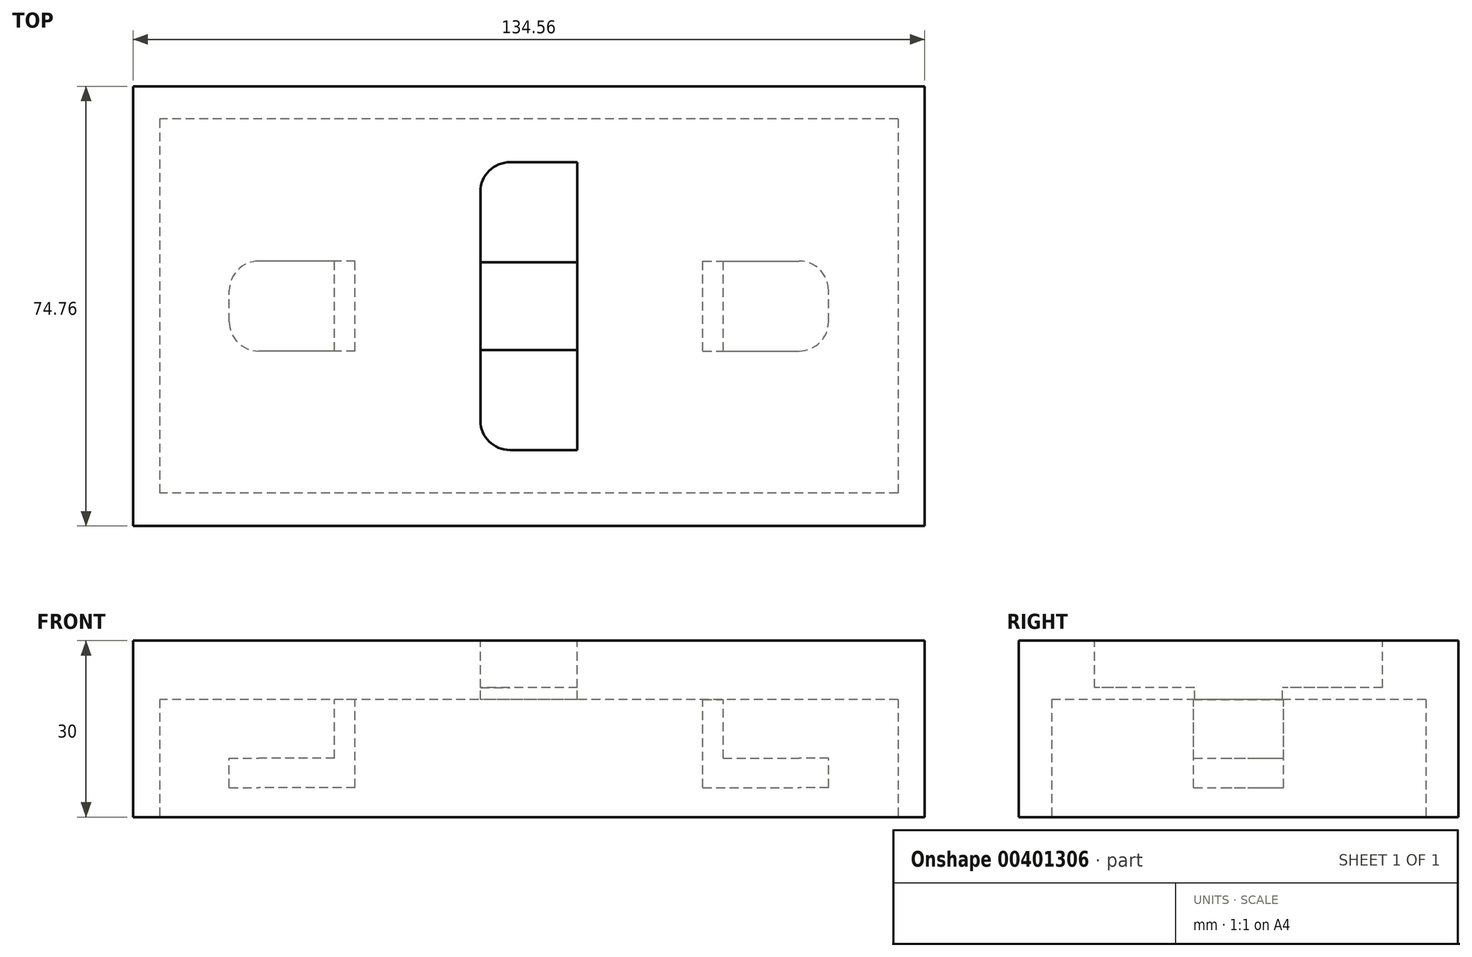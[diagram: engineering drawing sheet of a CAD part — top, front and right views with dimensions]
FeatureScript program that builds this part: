
annotation { "Feature Type Name" : "Feature", "Feature Type Description" : "" }
export const myFeature = defineFeature(function(context is Context, id is Id, definition is map)
    precondition{}
    {
        {
            var Q0;
            Q0=qCreatedBy(makeId("Top.planeOp"),FACE);
            var sketch = newSketch(context, id + "F0", { "sketchPlane" : qUnion([Q0])});
            skLineSegment(sketch, "E0.bottom", {"start": v(67.28, 37.38) * mm, "end": v(-67.28, 37.38) * mm});
            skLineSegment(sketch, "E0.top", {"start": v(67.28, -37.38) * mm, "end": v(-67.28, -37.38) * mm});
            skLineSegment(sketch, "E0.left", {"start": v(67.28, 37.38) * mm, "end": v(67.28, -37.38) * mm});
            skLineSegment(sketch, "E0.right", {"start": v(-67.28, 37.38) * mm, "end": v(-67.28, -37.38) * mm});
            skPoint(sketch, "E0.middle", {"position": v(0, 0) * mm});
            skSolve(sketch);
        }
        {
            var Q0;
            Q0=qSketchRegion(id+"F0",true);
            extrude(context, id + "F1", {"entities" : qUnion([Q0]), "depth" : 30 * mm});
        }
        {
            var Q0;
            Q0=makeQuery(id+"F1.opExtrude","CAP_FACE",FACE,{"disambiguationData":[OSD([sQuery(id+"F0.wireOp",EDGE,"E0.bottom"),sQuery(id+"F0.wireOp",EDGE,"E0.top"),sQuery(id+"F0.wireOp",EDGE,"E0.left"),sQuery(id+"F0.wireOp",EDGE,"E0.right")])],"isStart":false});
            var sketch = newSketch(context, id + "F2", { "sketchPlane" : qUnion([Q0])});
            skLineSegment(sketch, "E1.bottom", {"start": v(8.23, 24.47) * mm, "end": v(-3.23, 24.47) * mm});
            skLineSegment(sketch, "E1.top", {"start": v(8.23, -24.47) * mm, "end": v(-3.23, -24.47) * mm});
            skLineSegment(sketch, "E1.left", {"start": v(8.23, 24.47) * mm, "end": v(8.23, -24.47) * mm});
            skLineSegment(sketch, "E1.right", {"start": v(-8.23, 19.47) * mm, "end": v(-8.23, -19.47) * mm});
            skPoint(sketch, "E1.middle", {"position": v(0, 0) * mm});
            skPoint(sketch, "E2.visualSharp", {"position": v(-8.23, 24.47) * mm});
            skArc(sketch, "E2.filletArc", {"start": v(-3.23, 24.47) * mm, "mid": v(-6.77, 23) * mm, "end": v(-8.23, 19.47) * mm});
            skPoint(sketch, "E3.visualSharp", {"position": v(-8.23, -24.47) * mm});
            skArc(sketch, "E3.filletArc", {"start": v(-8.23, -19.47) * mm, "mid": v(-6.77, -23) * mm, "end": v(-3.23, -24.47) * mm});
            skSolve(sketch);
        }
        {
            var Q0;
            Q0=qSketchRegion(id+"F2",true);
            extrude(context, id + "F3", {"entities" : qUnion([Q0]), "operationType" : NewBodyOperationType.REMOVE, "oppositeDirection" : true, "depth" : 8 * mm});
        }
        {
            var Q0;
            Q0=makeQuery(id+"F1.opExtrude","CAP_FACE",FACE,{"disambiguationData":[OSD([sQuery(id+"F0.wireOp",EDGE,"E0.bottom"),sQuery(id+"F0.wireOp",EDGE,"E0.top"),sQuery(id+"F0.wireOp",EDGE,"E0.left"),sQuery(id+"F0.wireOp",EDGE,"E0.right")])],"isStart":true});
            var sketch = newSketch(context, id + "F4", { "sketchPlane" : qUnion([Q0])});
            skLineSegment(sketch, "E4.bottom", {"start": v(62.76, -31.81) * mm, "end": v(-62.76, -31.81) * mm});
            skLineSegment(sketch, "E4.top", {"start": v(62.76, 31.81) * mm, "end": v(-62.76, 31.81) * mm});
            skLineSegment(sketch, "E4.left", {"start": v(62.76, -31.81) * mm, "end": v(62.76, 31.81) * mm});
            skLineSegment(sketch, "E4.right", {"start": v(-62.76, -31.81) * mm, "end": v(-62.76, 31.81) * mm});
            skPoint(sketch, "E4.middle", {"position": v(0, 0) * mm});
            skSolve(sketch);
        }
        {
            var Q0;
            Q0=qSketchRegion(id+"F4",true);
            extrude(context, id + "F5", {"entities" : qUnion([Q0]), "operationType" : NewBodyOperationType.REMOVE, "oppositeDirection" : true, "depth" : 20 * mm});
        }
        {
            var Q0;
            Q0=makeQuery(id+"F3.boolean.opBoolean","COPY",FACE,{"derivedFrom":makeQuery(id+"F3.opExtrude","CAP_FACE",FACE,{"disambiguationData":[OSD([sQuery(id+"F2.wireOp",EDGE,"E1.bottom"),sQuery(id+"F2.wireOp",EDGE,"E1.top"),sQuery(id+"F2.wireOp",EDGE,"E1.left"),sQuery(id+"F2.wireOp",EDGE,"E1.right"),sQuery(id+"F2.wireOp",EDGE,"E2.filletArc"),sQuery(id+"F2.wireOp",EDGE,"E3.filletArc")])],"isStart":false})});
            var sketch = newSketch(context, id + "F6", { "sketchPlane" : qUnion([Q0])});
            skLineSegment(sketch, "E5.bottom", {"start": v(8.23, -7.48) * mm, "end": v(-8.23, -7.48) * mm});
            skLineSegment(sketch, "E5.top", {"start": v(8.23, 7.48) * mm, "end": v(-8.23, 7.48) * mm});
            skLineSegment(sketch, "E5.left", {"start": v(8.23, -7.48) * mm, "end": v(8.23, 7.48) * mm});
            skLineSegment(sketch, "E5.right", {"start": v(-8.23, -7.48) * mm, "end": v(-8.23, 7.48) * mm});
            skPoint(sketch, "E5.middle", {"position": v(0, 0) * mm});
            skSolve(sketch);
        }
        {
            var Q0;
            Q0=qSketchRegion(id+"F6",true);
            extrude(context, id + "F7", {"entities" : qUnion([Q0]), "operationType" : NewBodyOperationType.REMOVE, "endBound" : BoundingType.UP_TO_NEXT, "oppositeDirection" : true, "depth" : 25 * mm});
        }
        {
            var Q0;
            Q0=makeQuery(id+"F5.boolean.opBoolean","COPY",FACE,{"derivedFrom":makeQuery(id+"F5.opExtrude","CAP_FACE",FACE,{"disambiguationData":[OSD([sQuery(id+"F4.wireOp",EDGE,"E4.bottom"),sQuery(id+"F4.wireOp",EDGE,"E4.top"),sQuery(id+"F4.wireOp",EDGE,"E4.left"),sQuery(id+"F4.wireOp",EDGE,"E4.right")])],"isStart":false})});
            var sketch = newSketch(context, id + "F8", { "sketchPlane" : qUnion([Q0])});
            skLineSegment(sketch, "E6.bottom", {"start": v(-29.55, 7.65) * mm, "end": v(-33.03, 7.65) * mm});
            skLineSegment(sketch, "E6.top", {"start": v(-29.55, -7.65) * mm, "end": v(-33.03, -7.65) * mm});
            skLineSegment(sketch, "E6.left", {"start": v(-29.55, 7.65) * mm, "end": v(-29.55, -7.65) * mm});
            skLineSegment(sketch, "E6.right", {"start": v(-33.03, 7.65) * mm, "end": v(-33.03, -7.65) * mm});
            skPoint(sketch, "E6.middle", {"position": v(-31.3, 0) * mm});
            skPoint(sketch, "E7.MirrorP", {"position": v(31.3, 0) * mm});
            skLineSegment(sketch, "E8.MirrorCS", {"start": v(33.03, 7.65) * mm, "end": v(33.03, -7.65) * mm});
            skLineSegment(sketch, "E9.MirrorCS", {"start": v(29.55, 7.65) * mm, "end": v(29.55, -7.65) * mm});
            skLineSegment(sketch, "E10.MirrorCS", {"start": v(29.55, 7.65) * mm, "end": v(33.03, 7.65) * mm});
            skLineSegment(sketch, "E11.MirrorCS", {"start": v(29.55, -7.65) * mm, "end": v(33.03, -7.65) * mm});
            skSolve(sketch);
        }
        {
            var Q0;
            Q0=qSketchRegion(id+"F8",true);
            extrude(context, id + "F9", {"entities" : qUnion([Q0]), "operationType" : NewBodyOperationType.ADD, "depth" : 10 * mm});
        }
        {
            var Q0;
            Q0=makeQuery(id+"F9.opExtrude","CAP_FACE",FACE,{"disambiguationData":[OSD([sQuery(id+"F8.wireOp",EDGE,"E6.bottom"),sQuery(id+"F8.wireOp",EDGE,"E6.top"),sQuery(id+"F8.wireOp",EDGE,"E6.left"),sQuery(id+"F8.wireOp",EDGE,"E6.right")])],"isStart":false});
            var sketch = newSketch(context, id + "F10", { "sketchPlane" : qUnion([Q0])});
            skLineSegment(sketch, "E12.bottom", {"start": v(-29.55, 7.65) * mm, "end": v(-50.94, 7.65) * mm});
            skLineSegment(sketch, "E12.top", {"start": v(-29.55, -7.65) * mm, "end": v(-50.94, -7.65) * mm});
            skLineSegment(sketch, "E12.left", {"start": v(-29.55, 7.65) * mm, "end": v(-29.55, -7.65) * mm});
            skLineSegment(sketch, "E12.right", {"start": v(-50.94, 7.65) * mm, "end": v(-50.94, -7.65) * mm});
            skLineSegment(sketch, "E13.MirrorCS", {"start": v(50.94, 7.65) * mm, "end": v(50.94, -7.65) * mm});
            skLineSegment(sketch, "E14.MirrorCS", {"start": v(29.55, 7.65) * mm, "end": v(29.55, -7.65) * mm});
            skLineSegment(sketch, "E15.MirrorCS", {"start": v(29.55, -7.65) * mm, "end": v(50.94, -7.65) * mm});
            skLineSegment(sketch, "E16.MirrorCS", {"start": v(29.55, 7.65) * mm, "end": v(50.94, 7.65) * mm});
            skSolve(sketch);
        }
        {
            var Q0;
            Q0=qSketchRegion(id+"F10",true);
            extrude(context, id + "F11", {"entities" : qUnion([Q0]), "operationType" : NewBodyOperationType.ADD, "depth" : 5 * mm});
        }
        {
            var Q0;
            Q0=makeQuery(id+"F11.opExtrude","SWEPT_EDGE",EDGE,{"disambiguationData":[OSD([sQuery(id+"F10.wireOp",EDGE,"E12.bottom"),sQuery(id+"F10.wireOp",EDGE,"E12.right")])]});
            var Q1;
            Q1=makeQuery(id+"F11.opExtrude","SWEPT_EDGE",EDGE,{"disambiguationData":[OSD([sQuery(id+"F10.wireOp",EDGE,"E12.top"),sQuery(id+"F10.wireOp",EDGE,"E12.right")])]});
            var Q2;
            Q2=makeQuery(id+"F11.opExtrude","SWEPT_EDGE",EDGE,{"disambiguationData":[OSD([sQuery(id+"F10.wireOp",EDGE,"E13.MirrorCS"),sQuery(id+"F10.wireOp",EDGE,"E15.MirrorCS")])]});
            var Q3;
            Q3=makeQuery(id+"F11.opExtrude","SWEPT_EDGE",EDGE,{"disambiguationData":[OSD([sQuery(id+"F10.wireOp",EDGE,"E13.MirrorCS"),sQuery(id+"F10.wireOp",EDGE,"E16.MirrorCS")])]});
            fillet(context, id + "F12", {"entities" : qUnion([Q0, Q1, Q2, Q3]), "radius" : 5 * mm, "tangentPropagation" : true, "allowEdgeOverflow" : false});
        }
    });
